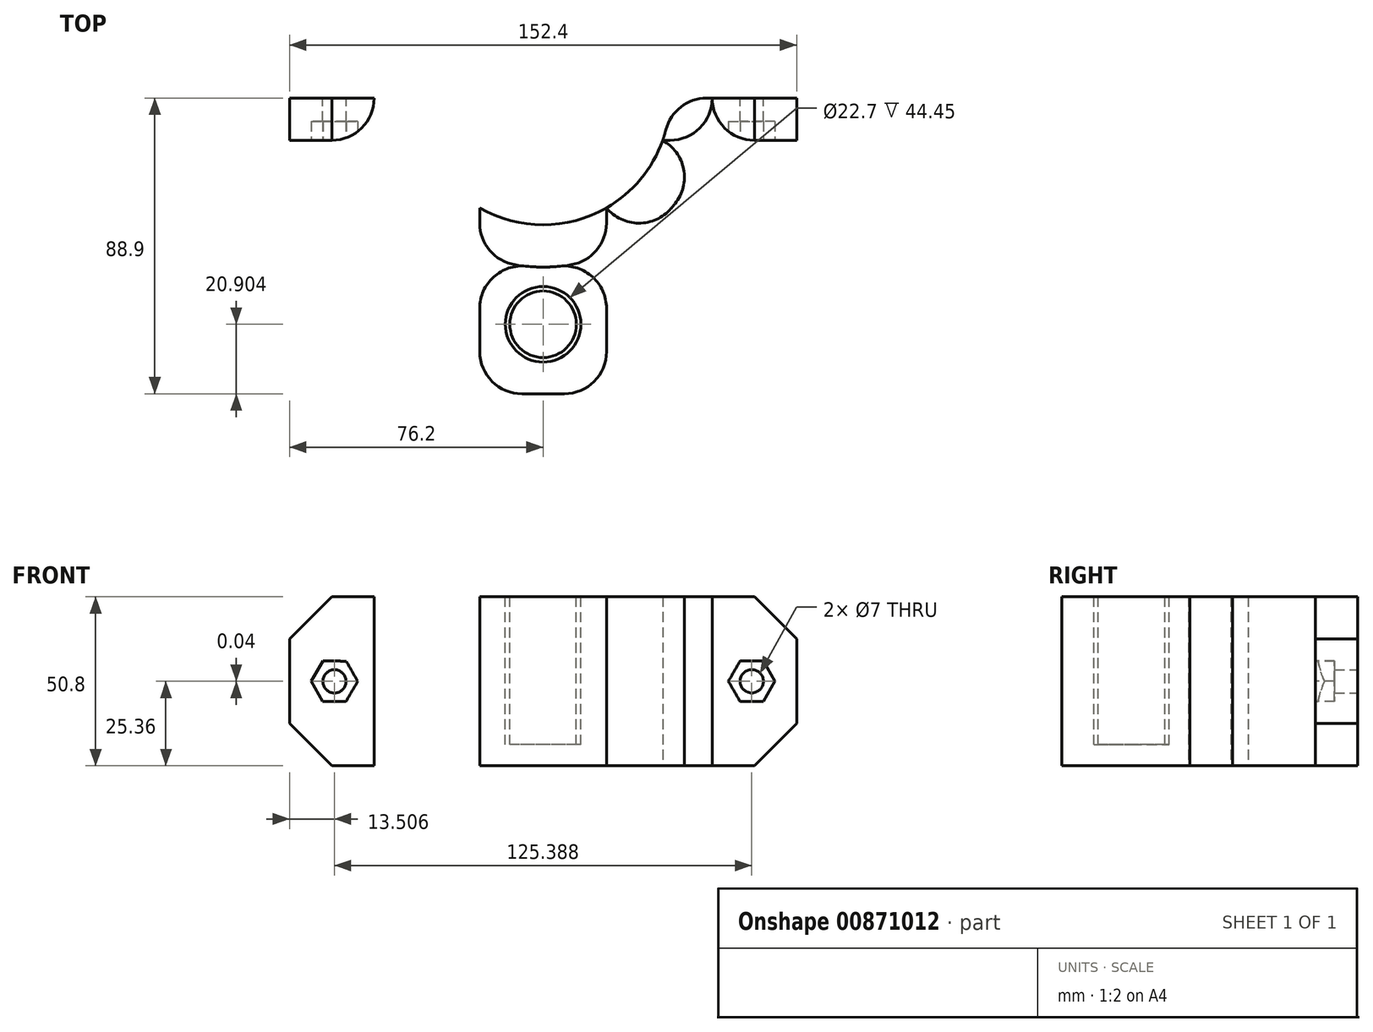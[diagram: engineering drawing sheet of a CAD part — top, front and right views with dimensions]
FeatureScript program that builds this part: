
annotation { "Feature Type Name" : "Feature", "Feature Type Description" : "" }
export const myFeature = defineFeature(function(context is Context, id is Id, definition is map)
    precondition{}
    {
        {
            var Q0;
            Q0=qCreatedBy(makeId("Top.planeOp"),FACE);
            var sketch = newSketch(context, id + "F0", { "sketchPlane" : qUnion([Q0])});
            skCircle(sketch, "E0", {"center": v(0, 0) * mm, "radius": 38.1 * mm});
            skCircle(sketch, "E1", {"center": v(0, 0) * mm, "radius": 50.8 * mm});
            skLineSegment(sketch, "E2.bottom", {"start": v(76.2, -12.7) * mm, "end": v(-76.2, -12.7) * mm});
            skLineSegment(sketch, "E2.top", {"start": v(76.2, 12.7) * mm, "end": v(-76.2, 12.7) * mm});
            skLineSegment(sketch, "E2.left", {"start": v(76.2, -12.7) * mm, "end": v(76.2, 12.7) * mm});
            skLineSegment(sketch, "E2.right", {"start": v(-76.2, -12.7) * mm, "end": v(-76.2, 12.7) * mm});
            skPoint(sketch, "E3", {"position": v(0, -50.8) * mm});
            skLineSegment(sketch, "E4.bottom", {"start": v(19.05, -12.7) * mm, "end": v(-19.05, -12.7) * mm});
            skLineSegment(sketch, "E4.top", {"start": v(19.05, -88.9) * mm, "end": v(-19.05, -88.9) * mm});
            skLineSegment(sketch, "E4.left", {"start": v(19.05, -12.7) * mm, "end": v(19.05, -88.9) * mm});
            skLineSegment(sketch, "E4.right", {"start": v(-19.05, -12.7) * mm, "end": v(-19.05, -88.9) * mm});
            skSolve(sketch);
        }
        {
            var Q0;
            {var subQ0=sQuery(id+"F0.wireOp",EDGE,"E2.top");var subQ1=sQuery(id+"F0.wireOp",EDGE,"E0");var subQ2=makeQuery(id+"F0.imprint","INTERSECT",VERTEX,{"disambiguationData":[OD(0.0)],"derivedFrom":[subQ1,subQ0]});Q0=makeQuery(id+"F0.imprint","IMPRINT",FACE,{"disambiguationData":[TD([[makeQuery(id+"F0.imprint","IMPRINT",EDGE,{"disambiguationData":[TD([[subQ2,1.0]])],"derivedFrom":subQ1}),-1.0]])]});}
            var Q1;
            {var subQ5=sQuery(id+"F0.wireOp",EDGE,"E2.right");Q1=makeQuery(id+"F0.imprint","IMPRINT",FACE,{"disambiguationData":[TD([[makeQuery(id+"F0.imprint","IMPRINT",EDGE,{"derivedFrom":subQ5}),-1.0]])]});}
            var Q2;
            {var subQ0=sQuery(id+"F0.wireOp",EDGE,"E2.top");var subQ1=sQuery(id+"F0.wireOp",EDGE,"E0");var subQ2=makeQuery(id+"F0.imprint","INTERSECT",VERTEX,{"disambiguationData":[OD(0.0)],"derivedFrom":[subQ1,subQ0]});Q2=makeQuery(id+"F0.imprint","IMPRINT",FACE,{"disambiguationData":[TD([[makeQuery(id+"F0.imprint","IMPRINT",EDGE,{"disambiguationData":[TD([[subQ2,-1.0]])],"derivedFrom":subQ1}),-1.0]])]});}
            var Q3;
            {var subQ0=sQuery(id+"F0.wireOp",EDGE,"E2.top");var subQ1=sQuery(id+"F0.wireOp",EDGE,"E0");var subQ2=makeQuery(id+"F0.imprint","INTERSECT",VERTEX,{"disambiguationData":[OD(1.0)],"derivedFrom":[subQ1,subQ0]});Q3=makeQuery(id+"F0.imprint","IMPRINT",FACE,{"disambiguationData":[TD([[makeQuery(id+"F0.imprint","IMPRINT",EDGE,{"disambiguationData":[TD([[subQ2,1.0]])],"derivedFrom":subQ1}),-1.0]])]});}
            var Q4;
            {var subQ5=sQuery(id+"F0.wireOp",EDGE,"E2.left");Q4=makeQuery(id+"F0.imprint","IMPRINT",FACE,{"disambiguationData":[TD([[makeQuery(id+"F0.imprint","IMPRINT",EDGE,{"derivedFrom":subQ5}),1.0]])]});}
            var Q5;
            {var subQ0=sQuery(id+"F0.wireOp",EDGE,"E2.bottom");var subQ1=sQuery(id+"F0.wireOp",EDGE,"E0");var subQ2=makeQuery(id+"F0.imprint","INTERSECT",VERTEX,{"disambiguationData":[OD(0.0)],"derivedFrom":[subQ1,subQ0]});Q5=makeQuery(id+"F0.imprint","IMPRINT",FACE,{"disambiguationData":[TD([[makeQuery(id+"F0.imprint","IMPRINT",EDGE,{"disambiguationData":[TD([[subQ2,-1.0]])],"derivedFrom":subQ1}),-1.0]])]});}
            var Q6;
            {var subQ0=sQuery(id+"F0.wireOp",EDGE,"E4.left");var subQ1=sQuery(id+"F0.wireOp",EDGE,"E0");var subQ2=makeQuery(id+"F0.imprint","INTERSECT",VERTEX,{"derivedFrom":[subQ1,subQ0]});Q6=makeQuery(id+"F0.imprint","IMPRINT",FACE,{"disambiguationData":[TD([[makeQuery(id+"F0.imprint","IMPRINT",EDGE,{"disambiguationData":[TD([[subQ2,-1.0]])],"derivedFrom":subQ1}),-1.0]])]});}
            var Q7;
            {var subQ0=sQuery(id+"F0.wireOp",EDGE,"E4.right");var subQ1=sQuery(id+"F0.wireOp",EDGE,"E0");var subQ2=makeQuery(id+"F0.imprint","INTERSECT",VERTEX,{"derivedFrom":[subQ1,subQ0]});Q7=makeQuery(id+"F0.imprint","IMPRINT",FACE,{"disambiguationData":[TD([[makeQuery(id+"F0.imprint","IMPRINT",EDGE,{"disambiguationData":[TD([[subQ2,-1.0]])],"derivedFrom":subQ1}),-1.0]])]});}
            var Q8;
            {var subQ5=sQuery(id+"F0.wireOp",EDGE,"E4.top");Q8=makeQuery(id+"F0.imprint","IMPRINT",FACE,{"disambiguationData":[TD([[makeQuery(id+"F0.imprint","IMPRINT",EDGE,{"derivedFrom":subQ5}),-1.0]])]});}
            extrude(context, id + "F1", {"entities" : qUnion([Q0, Q1, Q2, Q3, Q4, Q5, Q6, Q7, Q8]), "depth" : 50.8 * mm, "offsetDistance" : 25 * mm});
        }
        {
            var Q0;
            {var subQ0=sQuery(id+"F0.wireOp",EDGE,"E2.bottom");Q0=makeQuery(id+"F1.opExtrude","SWEPT_FACE",FACE,{"disambiguationData":[OSD([subQ0]),TDD([makeQuery(id+"F0.imprint","IMPRINT",EDGE,{"disambiguationData":[TD([[makeQuery(id+"F0.imprint","INTERSECT",VERTEX,{"derivedFrom":[subQ0,sQuery(id+"F0.wireOp",EDGE,"E2.right")]}),1.0]])],"derivedFrom":subQ0})])]});}
            var sketch = newSketch(context, id + "F2", { "sketchPlane" : qUnion([Q0])});
            skPoint(sketch, "E5", {"position": v(-62.7, 25.4) * mm});
            skPoint(sketch, "E5.positionSnap0", {"position": v(-76.2, 25.4) * mm});
            skPoint(sketch, "E5.positionSnap1", {"position": v(-62.7, 50.8) * mm});
            skPoint(sketch, "E6", {"position": v(62.7, 25.4) * mm});
            skCircle(sketch, "E7.cCircle", {"center": v(-62.7, 25.4) * mm, "radius": 7 * mm, "construction": true});
            skLineSegment(sketch, "E7.0", {"start": v(-59.16, 31.44) * mm, "end": v(-55.7, 25.36) * mm});
            skLineSegment(sketch, "E7.1", {"start": v(-55.7, 25.36) * mm, "end": v(-59.23, 19.32) * mm});
            skLineSegment(sketch, "E7.2", {"start": v(-59.23, 19.32) * mm, "end": v(-66.23, 19.36) * mm});
            skLineSegment(sketch, "E7.3", {"start": v(-66.23, 19.36) * mm, "end": v(-69.7, 25.44) * mm});
            skLineSegment(sketch, "E7.4", {"start": v(-69.7, 25.44) * mm, "end": v(-66.16, 31.48) * mm});
            skLineSegment(sketch, "E7.5", {"start": v(-66.16, 31.48) * mm, "end": v(-59.16, 31.44) * mm});
            skCircle(sketch, "E8.cCircle", {"center": v(62.7, 25.4) * mm, "radius": 7 * mm, "construction": true});
            skLineSegment(sketch, "E8.0", {"start": v(55.7, 25.4) * mm, "end": v(59.2, 31.46) * mm});
            skLineSegment(sketch, "E8.1", {"start": v(59.2, 31.46) * mm, "end": v(66.2, 31.46) * mm});
            skLineSegment(sketch, "E8.2", {"start": v(66.2, 31.46) * mm, "end": v(69.7, 25.4) * mm});
            skLineSegment(sketch, "E8.3", {"start": v(69.7, 25.4) * mm, "end": v(66.2, 19.34) * mm});
            skLineSegment(sketch, "E8.4", {"start": v(66.2, 19.34) * mm, "end": v(59.2, 19.34) * mm});
            skLineSegment(sketch, "E8.5", {"start": v(59.2, 19.34) * mm, "end": v(55.7, 25.4) * mm});
            skSolve(sketch);
        }
        {
            var Q0;
            Q0=qSketchRegion(id+"F2",true);
            extrude(context, id + "F3", {"entities" : qUnion([Q0]), "operationType" : NewBodyOperationType.REMOVE, "oppositeDirection" : true, "depth" : 12.7 * mm, "offsetDistance" : 25 * mm});
        }
        {
            var Q0;
            Q0=makeQuery(id+"F1.opExtrude","CAP_EDGE",EDGE,{"disambiguationData":[OSD([sQuery(id+"F0.wireOp",EDGE,"E2.right")])],"isStart":false});
            var Q1;
            Q1=makeQuery(id+"F1.opExtrude","CAP_EDGE",EDGE,{"disambiguationData":[OSD([sQuery(id+"F0.wireOp",EDGE,"E2.right")])],"isStart":true});
            var Q2;
            Q2=makeQuery(id+"F1.opExtrude","CAP_EDGE",EDGE,{"disambiguationData":[OSD([sQuery(id+"F0.wireOp",EDGE,"E2.left")])],"isStart":false});
            var Q3;
            Q3=makeQuery(id+"F1.opExtrude","CAP_EDGE",EDGE,{"disambiguationData":[OSD([sQuery(id+"F0.wireOp",EDGE,"E2.left")])],"isStart":true});
            chamfer(context, id + "F4", {"entities" : qUnion([Q0, Q1, Q2, Q3]), "width" : 12.7 * mm, "tangentPropagation" : true});
        }
        {
            var Q0;
            Q0=makeQuery(id+"F1.opExtrude","CAP_FACE",FACE,{"disambiguationData":[OSD([sQuery(id+"F0.wireOp",EDGE,"E0"),sQuery(id+"F0.wireOp",EDGE,"E1"),sQuery(id+"F0.wireOp",EDGE,"E2.bottom"),sQuery(id+"F0.wireOp",EDGE,"E2.top"),sQuery(id+"F0.wireOp",EDGE,"E2.left"),sQuery(id+"F0.wireOp",EDGE,"E2.right"),sQuery(id+"F0.wireOp",EDGE,"E4.top"),sQuery(id+"F0.wireOp",EDGE,"E4.left"),sQuery(id+"F0.wireOp",EDGE,"E4.right")])],"isStart":false});
            var sketch = newSketch(context, id + "F5", { "sketchPlane" : qUnion([Q0])});
            skPoint(sketch, "E9", {"position": v(0, -68) * mm});
            skPoint(sketch, "E9.positionSnap0", {"position": v(-19.05, -68) * mm});
            skPoint(sketch, "E9.positionSnap1", {"position": v(0, -88.9) * mm});
            skCircle(sketch, "E10", {"center": v(0, -68) * mm, "radius": 11.35 * mm});
            skCircle(sketch, "E11", {"center": v(0, -68) * mm, "radius": 10 * mm});
            skSolve(sketch);
        }
        {
            var Q0;
            Q0=makeQuery(id+"F5.imprint","IMPRINT",FACE,{"disambiguationData":[TD([[makeQuery(id+"F5.imprint","IMPRINT",EDGE,{"derivedFrom":sQuery(id+"F5.wireOp",EDGE,"E10")}),1.0]])]});
            var Q1;
            Q1=sQuery(id+"F5.wireOp",EDGE,"E11");
            var Q2;
            Q2=sQuery(id+"F5.wireOp",EDGE,"E10");
            extrude(context, id + "F6", {"entities" : qUnion([Q0]), "operationType" : NewBodyOperationType.REMOVE, "surfaceEntities" : qUnion([Q1, Q2]), "oppositeDirection" : true, "depth" : 44.45 * mm, "offsetDistance" : 25 * mm});
        }
        {
            var Q0;
            Q0=makeQuery(id+"F1.opExtrude","SWEPT_EDGE",EDGE,{"disambiguationData":[OSD([sQuery(id+"F0.wireOp",EDGE,"E4.top"),sQuery(id+"F0.wireOp",EDGE,"E4.right")])]});
            var Q1;
            Q1=makeQuery(id+"F1.opExtrude","SWEPT_EDGE",EDGE,{"disambiguationData":[OSD([sQuery(id+"F0.wireOp",EDGE,"E4.top"),sQuery(id+"F0.wireOp",EDGE,"E4.left")])]});
            var Q2;
            Q2=makeQuery(id+"F1.opExtrude","SWEPT_EDGE",EDGE,{"disambiguationData":[OSD([sQuery(id+"F0.wireOp",EDGE,"E1"),sQuery(id+"F0.wireOp",EDGE,"E4.right")])]});
            var Q3;
            Q3=makeQuery(id+"F1.opExtrude","SWEPT_EDGE",EDGE,{"disambiguationData":[OSD([sQuery(id+"F0.wireOp",EDGE,"E1"),sQuery(id+"F0.wireOp",EDGE,"E4.left")])]});
            var Q4;
            {var subQ0=sQuery(id+"F0.wireOp",EDGE,"E2.bottom");var subQ1=sQuery(id+"F0.wireOp",EDGE,"E1");Q4=makeQuery(id+"F1.opExtrude","SWEPT_EDGE",EDGE,{"disambiguationData":[OSD([subQ1,subQ0]),TDD([makeQuery(id+"F0.imprint","INTERSECT",VERTEX,{"disambiguationData":[OD(1.0)],"derivedFrom":[subQ1,subQ0]})])]});}
            var Q5;
            {var subQ0=sQuery(id+"F0.wireOp",EDGE,"E2.bottom");var subQ1=sQuery(id+"F0.wireOp",EDGE,"E1");Q5=makeQuery(id+"F1.opExtrude","SWEPT_EDGE",EDGE,{"disambiguationData":[OSD([subQ1,subQ0]),TDD([makeQuery(id+"F0.imprint","INTERSECT",VERTEX,{"disambiguationData":[OD(0.0)],"derivedFrom":[subQ1,subQ0]})])]});}
            var Q6;
            {var subQ0=sQuery(id+"F0.wireOp",EDGE,"E2.top");var subQ1=sQuery(id+"F0.wireOp",EDGE,"E1");Q6=makeQuery(id+"F1.opExtrude","SWEPT_EDGE",EDGE,{"disambiguationData":[OSD([subQ1,subQ0]),TDD([makeQuery(id+"F0.imprint","INTERSECT",VERTEX,{"disambiguationData":[OD(1.0)],"derivedFrom":[subQ1,subQ0]})])]});}
            var Q7;
            {var subQ0=sQuery(id+"F0.wireOp",EDGE,"E2.top");var subQ1=sQuery(id+"F0.wireOp",EDGE,"E1");Q7=makeQuery(id+"F1.opExtrude","SWEPT_EDGE",EDGE,{"disambiguationData":[OSD([subQ1,subQ0]),TDD([makeQuery(id+"F0.imprint","INTERSECT",VERTEX,{"disambiguationData":[OD(0.0)],"derivedFrom":[subQ1,subQ0]})])]});}
            fillet(context, id + "F7", {"entities" : qUnion([Q0, Q1, Q2, Q3, Q4, Q5, Q6, Q7]), "radius" : 12.7 * mm, "tangentPropagation" : true, "allowEdgeOverflow" : false});
        }
        {
            var Q0;
            Q0=makeQuery(id+"F3.boolean.opBoolean","COPY",FACE,{"derivedFrom":makeQuery(id+"F3.opExtrude","CAP_FACE",FACE,{"disambiguationData":[OSD([sQuery(id+"F2.wireOp",EDGE,"E7.0"),sQuery(id+"F2.wireOp",EDGE,"E7.1"),sQuery(id+"F2.wireOp",EDGE,"E7.2"),sQuery(id+"F2.wireOp",EDGE,"E7.3"),sQuery(id+"F2.wireOp",EDGE,"E7.4"),sQuery(id+"F2.wireOp",EDGE,"E7.5")])],"isStart":false})});
            var sketch = newSketch(context, id + "F8", { "sketchPlane" : qUnion([Q0])});
            skPoint(sketch, "E12", {"position": v(-62.66, 25.44) * mm});
            skPoint(sketch, "E12.positionSnap0", {"position": v(-62.66, 31.46) * mm});
            skPoint(sketch, "E13", {"position": v(62.7, 25.44) * mm});
            skPoint(sketch, "E14", {"position": v(62.7, 31.46) * mm});
            skCircle(sketch, "E15", {"center": v(-62.66, 25.44) * mm, "radius": 3.5 * mm});
            skCircle(sketch, "E16", {"center": v(62.7, 25.44) * mm, "radius": 3.5 * mm});
            skSolve(sketch);
        }
        {
            var Q0;
            Q0=makeQuery(id+"F8.imprint","IMPRINT",FACE,{"disambiguationData":[TD([[makeQuery(id+"F8.imprint","IMPRINT",EDGE,{"derivedFrom":sQuery(id+"F8.wireOp",EDGE,"E15")}),1.0]])]});
            var Q1;
            Q1=makeQuery(id+"F8.imprint","IMPRINT",FACE,{"disambiguationData":[TD([[makeQuery(id+"F8.imprint","IMPRINT",EDGE,{"derivedFrom":sQuery(id+"F8.wireOp",EDGE,"E16")}),1.0]])]});
            extrude(context, id + "F9", {"entities" : qUnion([Q0, Q1]), "operationType" : NewBodyOperationType.REMOVE, "endBound" : BoundingType.THROUGH_ALL, "oppositeDirection" : true, "depth" : 25 * mm, "offsetDistance" : 25 * mm});
        }
        {
            var Q0;
            Q0=qCreatedBy(makeId("Front.planeOp"),FACE);
            var sketch = newSketch(context, id + "F10", { "sketchPlane" : qUnion([Q0])});
            skLineSegment(sketch, "E17.bottom", {"start": v(-97.94, 76.17) * mm, "end": v(85.9, 76.17) * mm});
            skLineSegment(sketch, "E17.top", {"start": v(-97.94, -81.22) * mm, "end": v(85.9, -81.22) * mm});
            skLineSegment(sketch, "E17.left", {"start": v(-97.94, 76.17) * mm, "end": v(-97.94, -81.22) * mm});
            skLineSegment(sketch, "E17.right", {"start": v(85.9, 76.17) * mm, "end": v(85.9, -81.22) * mm});
            skSolve(sketch);
        }
        {
            var Q0;
            Q0=qSketchRegion(id+"F10",true);
            extrude(context, id + "F11", {"entities" : qUnion([Q0]), "operationType" : NewBodyOperationType.REMOVE, "oppositeDirection" : true, "depth" : 63.5 * mm, "offsetDistance" : 25 * mm});
        }
        {
            var Q0;
            Q0=makeQuery(id+"F11.boolean.opBoolean","INTERSECT",EDGE,{"disambiguationData":[OD(0.0)],"derivedFrom":[makeQuery(id+"F1.opExtrude","SWEPT_FACE",FACE,{"disambiguationData":[OSD([sQuery(id+"F0.wireOp",EDGE,"E0")])]}),makeQuery(id+"F11.opExtrude","CAP_FACE",FACE,{"disambiguationData":[OSD([sQuery(id+"F10.wireOp",EDGE,"E17.bottom"),sQuery(id+"F10.wireOp",EDGE,"E17.top"),sQuery(id+"F10.wireOp",EDGE,"E17.left"),sQuery(id+"F10.wireOp",EDGE,"E17.right")])],"isStart":true})]});
            var Q1;
            Q1=makeQuery(id+"F11.boolean.opBoolean","INTERSECT",EDGE,{"disambiguationData":[OD(1.0)],"derivedFrom":[makeQuery(id+"F1.opExtrude","SWEPT_FACE",FACE,{"disambiguationData":[OSD([sQuery(id+"F0.wireOp",EDGE,"E0")])]}),makeQuery(id+"F11.opExtrude","CAP_FACE",FACE,{"disambiguationData":[OSD([sQuery(id+"F10.wireOp",EDGE,"E17.bottom"),sQuery(id+"F10.wireOp",EDGE,"E17.top"),sQuery(id+"F10.wireOp",EDGE,"E17.left"),sQuery(id+"F10.wireOp",EDGE,"E17.right")])],"isStart":true})]});
            fillet(context, id + "F12", {"entities" : qUnion([Q0, Q1]), "radius" : 12.7 * mm, "tangentPropagation" : true, "allowEdgeOverflow" : false});
        }
        {
            var Q0;
            {var subQ4=sQuery(id+"F0.wireOp",EDGE,"E2.left");Q0=makeQuery(id+"F11.boolean.opBoolean","COPY",FACE,{"disambiguationData":[TD([makeQuery(id+"F1.opExtrude","SWEPT_FACE",FACE,{"disambiguationData":[OSD([subQ4])]})])],"derivedFrom":makeQuery(id+"F11.opExtrude","CAP_FACE",FACE,{"disambiguationData":[OSD([sQuery(id+"F10.wireOp",EDGE,"E17.bottom"),sQuery(id+"F10.wireOp",EDGE,"E17.top"),sQuery(id+"F10.wireOp",EDGE,"E17.left"),sQuery(id+"F10.wireOp",EDGE,"E17.right")])],"isStart":true})});}
            var sketch = newSketch(context, id + "F13", { "sketchPlane" : qUnion([Q0])});
            skLineSegment(sketch, "E18.bottom", {"start": v(-71.5, 35.27) * mm, "end": v(-53.43, 35.27) * mm});
            skLineSegment(sketch, "E18.top", {"start": v(-71.5, 15.58) * mm, "end": v(-53.43, 15.58) * mm});
            skLineSegment(sketch, "E18.left", {"start": v(-71.5, 35.27) * mm, "end": v(-71.5, 15.58) * mm});
            skLineSegment(sketch, "E18.right", {"start": v(-53.43, 35.27) * mm, "end": v(-53.43, 15.58) * mm});
            skLineSegment(sketch, "E19.bottom", {"start": v(54.56, 33.66) * mm, "end": v(72.22, 33.66) * mm});
            skLineSegment(sketch, "E19.top", {"start": v(54.56, 15.58) * mm, "end": v(72.22, 15.58) * mm});
            skLineSegment(sketch, "E19.left", {"start": v(54.56, 33.66) * mm, "end": v(54.56, 15.58) * mm});
            skLineSegment(sketch, "E19.right", {"start": v(72.22, 33.66) * mm, "end": v(72.22, 15.58) * mm});
            skPoint(sketch, "E20", {"position": v(-62.7, 25.4) * mm});
            skPoint(sketch, "E20.positionSnap0", {"position": v(-62.7, 19.34) * mm});
            skPoint(sketch, "E21", {"position": v(62.66, 31.46) * mm});
            skLineSegment(sketch, "E22", {"start": v(63.76, 25.36) * mm, "end": v(55.7, 25.36) * mm, "construction": true});
            skPoint(sketch, "E23", {"position": v(62.73, 19.34) * mm});
            skLineSegment(sketch, "E24", {"start": v(62.66, 31.46) * mm, "end": v(62.73, 19.34) * mm, "construction": true});
            skPoint(sketch, "E25", {"position": v(62.7, 25.36) * mm});
            skCircle(sketch, "E26", {"center": v(62.7, 25.36) * mm, "radius": 3.5 * mm});
            skCircle(sketch, "E27", {"center": v(-62.7, 25.4) * mm, "radius": 3.5 * mm});
            skSolve(sketch);
        }
        {
            var Q0;
            Q0=makeQuery(id+"F13.imprint","IMPRINT",FACE,{"disambiguationData":[TD([[makeQuery(id+"F13.imprint","IMPRINT",EDGE,{"derivedFrom":sQuery(id+"F13.wireOp",EDGE,"E27")}),-1.0]])]});
            var Q1;
            Q1=makeQuery(id+"F13.imprint","IMPRINT",FACE,{"disambiguationData":[TD([[makeQuery(id+"F13.imprint","IMPRINT",EDGE,{"derivedFrom":sQuery(id+"F13.wireOp",EDGE,"E19.bottom")}),-1.0]])]});
            extrude(context, id + "F14", {"entities" : qUnion([Q0, Q1]), "operationType" : NewBodyOperationType.ADD, "oppositeDirection" : true, "depth" : 7 * mm, "offsetDistance" : 25 * mm});
        }
    });
